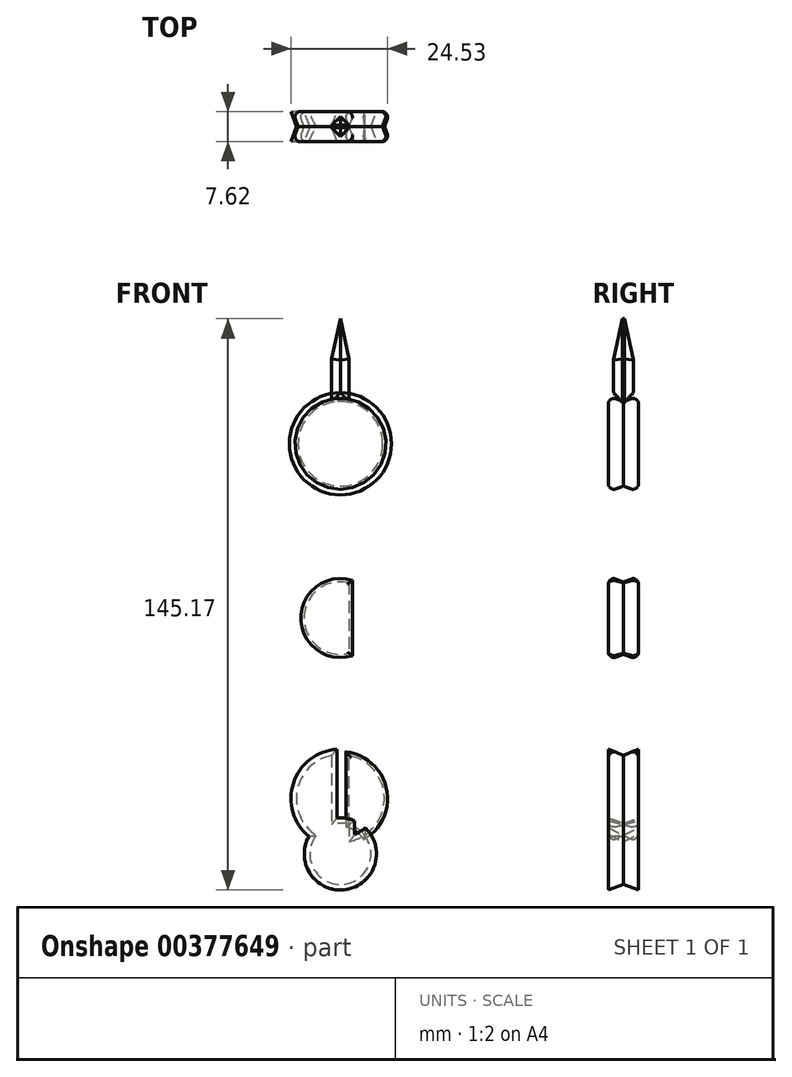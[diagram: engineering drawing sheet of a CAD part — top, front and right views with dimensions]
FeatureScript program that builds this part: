
annotation { "Feature Type Name" : "Feature", "Feature Type Description" : "" }
export const myFeature = defineFeature(function(context is Context, id is Id, definition is map)
    precondition{}
    {
        {
            var Q0;
            Q0=qCreatedBy(makeId("Front.planeOp"),FACE);
            var sketch = newSketch(context, id + "F0", { "sketchPlane" : qUnion([Q0])});
            skCircle(sketch, "E0", {"center": v(0, 0) * mm, "radius": 9.22 * mm});
            skCircle(sketch, "E1", {"center": v(0, -45.85) * mm, "radius": 11.17 * mm});
            skCircle(sketch, "E2", {"center": v(0, -59.93) * mm, "radius": 7.78 * mm});
            skCircle(sketch, "E3", {"center": v(0, 44.27) * mm, "radius": 10.75 * mm});
            skLineSegment(sketch, "E4.bottom", {"start": v(2.23, 65.82) * mm, "end": v(-2.23, 65.82) * mm});
            skLineSegment(sketch, "E4.top", {"start": v(2.23, -65.82) * mm, "end": v(-2.23, -65.82) * mm});
            skLineSegment(sketch, "E4.left", {"start": v(2.23, 65.82) * mm, "end": v(2.23, -65.82) * mm});
            skLineSegment(sketch, "E4.right", {"start": v(-2.23, 65.82) * mm, "end": v(-2.23, -65.82) * mm});
            skLineSegment(sketch, "E5", {"start": v(-2.23, 65.82) * mm, "end": v(0, 76.07) * mm});
            skLineSegment(sketch, "E6", {"start": v(0, 76.07) * mm, "end": v(2.23, 65.82) * mm});
            skSolve(sketch);
        }
        {
            var Q0;
            {var subQ5=sQuery(id+"F0.wireOp",EDGE,"E4.bottom");Q0=makeQuery(id+"F0.imprint","IMPRINT",FACE,{"disambiguationData":[TD([[makeQuery(id+"F0.imprint","IMPRINT",EDGE,{"derivedFrom":subQ5}),1.0]])]});}
            var Q1;
            Q1=makeQuery(id+"F0.imprint","IMPRINT",FACE,{"disambiguationData":[TD([[makeQuery(id+"F0.imprint","IMPRINT",EDGE,{"derivedFrom":sQuery(id+"F0.wireOp",EDGE,"E4.bottom")}),-1.0]])]});
            var Q2;
            {var subQ0=sQuery(id+"F0.wireOp",EDGE,"E4.right");var subQ1=sQuery(id+"F0.wireOp",EDGE,"E0");var subQ2=makeQuery(id+"F0.imprint","INTERSECT",VERTEX,{"disambiguationData":[OD(0.0)],"derivedFrom":[subQ1,subQ0]});Q2=makeQuery(id+"F0.imprint","IMPRINT",FACE,{"disambiguationData":[TD([[makeQuery(id+"F0.imprint","IMPRINT",EDGE,{"disambiguationData":[TD([[subQ2,1.0]])],"derivedFrom":subQ1}),-1.0]])]});}
            var Q3;
            {var subQ0=sQuery(id+"F0.wireOp",EDGE,"E4.right");var subQ1=sQuery(id+"F0.wireOp",EDGE,"E0");var subQ2=makeQuery(id+"F0.imprint","INTERSECT",VERTEX,{"disambiguationData":[OD(1.0)],"derivedFrom":[subQ1,subQ0]});Q3=makeQuery(id+"F0.imprint","IMPRINT",FACE,{"disambiguationData":[TD([[makeQuery(id+"F0.imprint","IMPRINT",EDGE,{"disambiguationData":[TD([[subQ2,-1.0]])],"derivedFrom":subQ1}),-1.0]])]});}
            extrude(context, id + "F1", {"entities" : qUnion([Q0, Q1, Q2, Q3]), "endBound" : BoundingType.SYMMETRIC, "depth" : 5.08 * mm});
        }
        {
            var Q0;
            Q0=makeQuery(id+"F1.opExtrude","CAP_FACE",FACE,{"disambiguationData":[OSD([sQuery(id+"F0.wireOp",EDGE,"E0"),sQuery(id+"F0.wireOp",EDGE,"E3"),sQuery(id+"F0.wireOp",EDGE,"E4.left"),sQuery(id+"F0.wireOp",EDGE,"E4.right")])],"isStart":false});
            var Q1;
            Q1=makeQuery(id+"F1.opExtrude","CAP_FACE",FACE,{"disambiguationData":[OSD([sQuery(id+"F0.wireOp",EDGE,"E3"),sQuery(id+"F0.wireOp",EDGE,"E4.left"),sQuery(id+"F0.wireOp",EDGE,"E4.right"),sQuery(id+"F0.wireOp",EDGE,"E5"),sQuery(id+"F0.wireOp",EDGE,"E6")])],"isStart":false});
            var Q2;
            Q2=makeQuery(id+"F1.opExtrude","CAP_FACE",FACE,{"disambiguationData":[OSD([sQuery(id+"F0.wireOp",EDGE,"E0"),sQuery(id+"F0.wireOp",EDGE,"E1"),sQuery(id+"F0.wireOp",EDGE,"E4.left"),sQuery(id+"F0.wireOp",EDGE,"E4.right")])],"isStart":false});
            var Q3;
            Q3=makeQuery(id+"F1.opExtrude","CAP_FACE",FACE,{"disambiguationData":[OSD([sQuery(id+"F0.wireOp",EDGE,"E0"),sQuery(id+"F0.wireOp",EDGE,"E1"),sQuery(id+"F0.wireOp",EDGE,"E4.left"),sQuery(id+"F0.wireOp",EDGE,"E4.right")])],"isStart":true});
            var Q4;
            Q4=makeQuery(id+"F1.opExtrude","CAP_FACE",FACE,{"disambiguationData":[OSD([sQuery(id+"F0.wireOp",EDGE,"E0"),sQuery(id+"F0.wireOp",EDGE,"E3"),sQuery(id+"F0.wireOp",EDGE,"E4.left"),sQuery(id+"F0.wireOp",EDGE,"E4.right")])],"isStart":true});
            var Q5;
            Q5=makeQuery(id+"F1.opExtrude","CAP_FACE",FACE,{"disambiguationData":[OSD([sQuery(id+"F0.wireOp",EDGE,"E3"),sQuery(id+"F0.wireOp",EDGE,"E4.left"),sQuery(id+"F0.wireOp",EDGE,"E4.right"),sQuery(id+"F0.wireOp",EDGE,"E5"),sQuery(id+"F0.wireOp",EDGE,"E6")])],"isStart":true});
            chamfer(context, id + "F2", {"entities" : qUnion([Q0, Q1, Q2, Q3, Q4, Q5]), "width" : 2.23 * mm, "tangentPropagation" : true});
        }
        {
            var Q0;
            {var subQ0=sQuery(id+"F0.wireOp",EDGE,"E4.right");var subQ1=sQuery(id+"F0.wireOp",EDGE,"E3");var subQ2=makeQuery(id+"F0.imprint","INTERSECT",VERTEX,{"disambiguationData":[OD(0.0)],"derivedFrom":[subQ1,subQ0]});Q0=makeQuery(id+"F0.imprint","IMPRINT",FACE,{"disambiguationData":[TD([[makeQuery(id+"F0.imprint","IMPRINT",EDGE,{"disambiguationData":[TD([[subQ2,-1.0]])],"derivedFrom":subQ1}),1.0]])]});}
            var Q1;
            {var subQ0=sQuery(id+"F0.wireOp",EDGE,"E4.right");var subQ1=sQuery(id+"F0.wireOp",EDGE,"E3");var subQ2=makeQuery(id+"F0.imprint","INTERSECT",VERTEX,{"disambiguationData":[OD(0.0)],"derivedFrom":[subQ1,subQ0]});Q1=makeQuery(id+"F0.imprint","IMPRINT",FACE,{"disambiguationData":[TD([[makeQuery(id+"F0.imprint","IMPRINT",EDGE,{"disambiguationData":[TD([[subQ2,1.0]])],"derivedFrom":subQ1}),1.0]])]});}
            var Q2;
            {var subQ0=sQuery(id+"F0.wireOp",EDGE,"E4.left");var subQ1=sQuery(id+"F0.wireOp",EDGE,"E3");var subQ2=makeQuery(id+"F0.imprint","INTERSECT",VERTEX,{"disambiguationData":[OD(0.0)],"derivedFrom":[subQ1,subQ0]});Q2=makeQuery(id+"F0.imprint","IMPRINT",FACE,{"disambiguationData":[TD([[makeQuery(id+"F0.imprint","IMPRINT",EDGE,{"disambiguationData":[TD([[subQ2,1.0]])],"derivedFrom":subQ1}),1.0]])]});}
            var Q3;
            {var subQ0=sQuery(id+"F0.wireOp",EDGE,"E4.right");var subQ1=sQuery(id+"F0.wireOp",EDGE,"E0");var subQ2=makeQuery(id+"F0.imprint","INTERSECT",VERTEX,{"disambiguationData":[OD(0.0)],"derivedFrom":[subQ1,subQ0]});Q3=makeQuery(id+"F0.imprint","IMPRINT",FACE,{"disambiguationData":[TD([[makeQuery(id+"F0.imprint","IMPRINT",EDGE,{"disambiguationData":[TD([[subQ2,-1.0]])],"derivedFrom":subQ1}),1.0]])]});}
            var Q4;
            {var subQ0=sQuery(id+"F0.wireOp",EDGE,"E4.left");var subQ1=sQuery(id+"F0.wireOp",EDGE,"E0");var subQ2=makeQuery(id+"F0.imprint","INTERSECT",VERTEX,{"disambiguationData":[OD(0.0)],"derivedFrom":[subQ1,subQ0]});Q4=makeQuery(id+"F0.imprint","IMPRINT",FACE,{"disambiguationData":[TD([[makeQuery(id+"F0.imprint","IMPRINT",EDGE,{"disambiguationData":[TD([[subQ2,1.0]])],"derivedFrom":subQ1}),1.0]])]});}
            var Q5;
            {var subQ0=sQuery(id+"F0.wireOp",EDGE,"E4.right");var subQ1=sQuery(id+"F0.wireOp",EDGE,"E0");var subQ2=makeQuery(id+"F0.imprint","INTERSECT",VERTEX,{"disambiguationData":[OD(0.0)],"derivedFrom":[subQ1,subQ0]});Q5=makeQuery(id+"F0.imprint","IMPRINT",FACE,{"disambiguationData":[TD([[makeQuery(id+"F0.imprint","IMPRINT",EDGE,{"disambiguationData":[TD([[subQ2,1.0]])],"derivedFrom":subQ1}),1.0]])]});}
            var Q6;
            {var subQ0=sQuery(id+"F0.wireOp",EDGE,"E4.right");var subQ1=sQuery(id+"F0.wireOp",EDGE,"E1");var subQ2=makeQuery(id+"F0.imprint","INTERSECT",VERTEX,{"disambiguationData":[OD(0.0)],"derivedFrom":[subQ1,subQ0]});Q6=makeQuery(id+"F0.imprint","IMPRINT",FACE,{"disambiguationData":[TD([[makeQuery(id+"F0.imprint","IMPRINT",EDGE,{"disambiguationData":[TD([[subQ2,-1.0]])],"derivedFrom":subQ1}),1.0]])]});}
            var Q7;
            {var subQ0=sQuery(id+"F0.wireOp",EDGE,"E4.right");var subQ1=sQuery(id+"F0.wireOp",EDGE,"E1");var subQ2=makeQuery(id+"F0.imprint","INTERSECT",VERTEX,{"disambiguationData":[OD(0.0)],"derivedFrom":[subQ1,subQ0]});Q7=makeQuery(id+"F0.imprint","IMPRINT",FACE,{"disambiguationData":[TD([[makeQuery(id+"F0.imprint","IMPRINT",EDGE,{"disambiguationData":[TD([[subQ2,1.0]])],"derivedFrom":subQ1}),1.0]])]});}
            var Q8;
            {var subQ0=sQuery(id+"F0.wireOp",EDGE,"E4.left");var subQ1=sQuery(id+"F0.wireOp",EDGE,"E1");var subQ2=makeQuery(id+"F0.imprint","INTERSECT",VERTEX,{"disambiguationData":[OD(0.0)],"derivedFrom":[subQ1,subQ0]});Q8=makeQuery(id+"F0.imprint","IMPRINT",FACE,{"disambiguationData":[TD([[makeQuery(id+"F0.imprint","IMPRINT",EDGE,{"disambiguationData":[TD([[subQ2,1.0]])],"derivedFrom":subQ1}),1.0]])]});}
            var Q9;
            {var subQ0=sQuery(id+"F0.wireOp",EDGE,"E4.top");Q9=makeQuery(id+"F0.imprint","IMPRINT",FACE,{"disambiguationData":[TD([[makeQuery(id+"F0.imprint","IMPRINT",EDGE,{"derivedFrom":subQ0}),1.0]])]});}
            var Q10;
            {var subQ5=sQuery(id+"F0.wireOp",EDGE,"E4.top");Q10=makeQuery(id+"F0.imprint","IMPRINT",FACE,{"disambiguationData":[TD([[makeQuery(id+"F0.imprint","IMPRINT",EDGE,{"derivedFrom":subQ5}),-1.0]])]});}
            var Q11;
            {var subQ0=sQuery(id+"F0.wireOp",EDGE,"E2");var subQ1=sQuery(id+"F0.wireOp",EDGE,"E1");var subQ2=makeQuery(id+"F0.imprint","INTERSECT",VERTEX,{"disambiguationData":[OD(1.0)],"derivedFrom":[subQ1,subQ0]});Q11=makeQuery(id+"F0.imprint","IMPRINT",FACE,{"disambiguationData":[TD([[makeQuery(id+"F0.imprint","IMPRINT",EDGE,{"disambiguationData":[TD([[subQ2,1.0]])],"derivedFrom":subQ1}),1.0]])]});}
            var Q12;
            {var subQ0=sQuery(id+"F0.wireOp",EDGE,"E4.right");var subQ1=sQuery(id+"F0.wireOp",EDGE,"E1");var subQ2=makeQuery(id+"F0.imprint","INTERSECT",VERTEX,{"disambiguationData":[OD(1.0)],"derivedFrom":[subQ1,subQ0]});Q12=makeQuery(id+"F0.imprint","IMPRINT",FACE,{"disambiguationData":[TD([[makeQuery(id+"F0.imprint","IMPRINT",EDGE,{"disambiguationData":[TD([[subQ2,-1.0]])],"derivedFrom":subQ1}),1.0]])]});}
            var Q13;
            {var subQ0=sQuery(id+"F0.wireOp",EDGE,"E2");var subQ1=sQuery(id+"F0.wireOp",EDGE,"E1");var subQ2=makeQuery(id+"F0.imprint","INTERSECT",VERTEX,{"disambiguationData":[OD(0.0)],"derivedFrom":[subQ1,subQ0]});Q13=makeQuery(id+"F0.imprint","IMPRINT",FACE,{"disambiguationData":[TD([[makeQuery(id+"F0.imprint","IMPRINT",EDGE,{"disambiguationData":[TD([[subQ2,-1.0]])],"derivedFrom":subQ1}),1.0]])]});}
            extrude(context, id + "F3", {"entities" : qUnion([Q0, Q1, Q2, Q3, Q4, Q5, Q6, Q7, Q8, Q9, Q10, Q11, Q12, Q13]), "endBound" : BoundingType.SYMMETRIC, "depth" : 7.62 * mm, "hasDraft" : true, "draftAngle" : 20 * degree});
        }
        {
            var Q0;
            Q0=makeQuery(id+"F3.opExtrude","CAP_FACE",FACE,{"disambiguationData":[OSD([sQuery(id+"F0.wireOp",EDGE,"E3")])],"isStart":false});
            var Q1;
            Q1=makeQuery(id+"F3.opExtrude","CAP_FACE",FACE,{"disambiguationData":[OSD([sQuery(id+"F0.wireOp",EDGE,"E0")])],"isStart":false});
            var Q2;
            Q2=makeQuery(id+"F3.opExtrude","CAP_FACE",FACE,{"disambiguationData":[OSD([sQuery(id+"F0.wireOp",EDGE,"E1"),sQuery(id+"F0.wireOp",EDGE,"E2")])],"isStart":false});
            var Q3;
            Q3=makeQuery(id+"F3.opExtrude","CAP_FACE",FACE,{"disambiguationData":[OSD([sQuery(id+"F0.wireOp",EDGE,"E1"),sQuery(id+"F0.wireOp",EDGE,"E2")])],"isStart":true});
            var Q4;
            Q4=makeQuery(id+"F3.opExtrude","CAP_FACE",FACE,{"disambiguationData":[OSD([sQuery(id+"F0.wireOp",EDGE,"E0")])],"isStart":true});
            var Q5;
            Q5=makeQuery(id+"F3.opExtrude","CAP_FACE",FACE,{"disambiguationData":[OSD([sQuery(id+"F0.wireOp",EDGE,"E3")])],"isStart":true});
            fillet(context, id + "F4", {"entities" : qUnion([Q0, Q1, Q2, Q3, Q4, Q5]), "radius" : 1.27 * mm, "tangentPropagation" : true, "rho" : 0.3, "crossSection" : FilletCrossSection.CONIC, "allowEdgeOverflow" : false});
        }
    });
